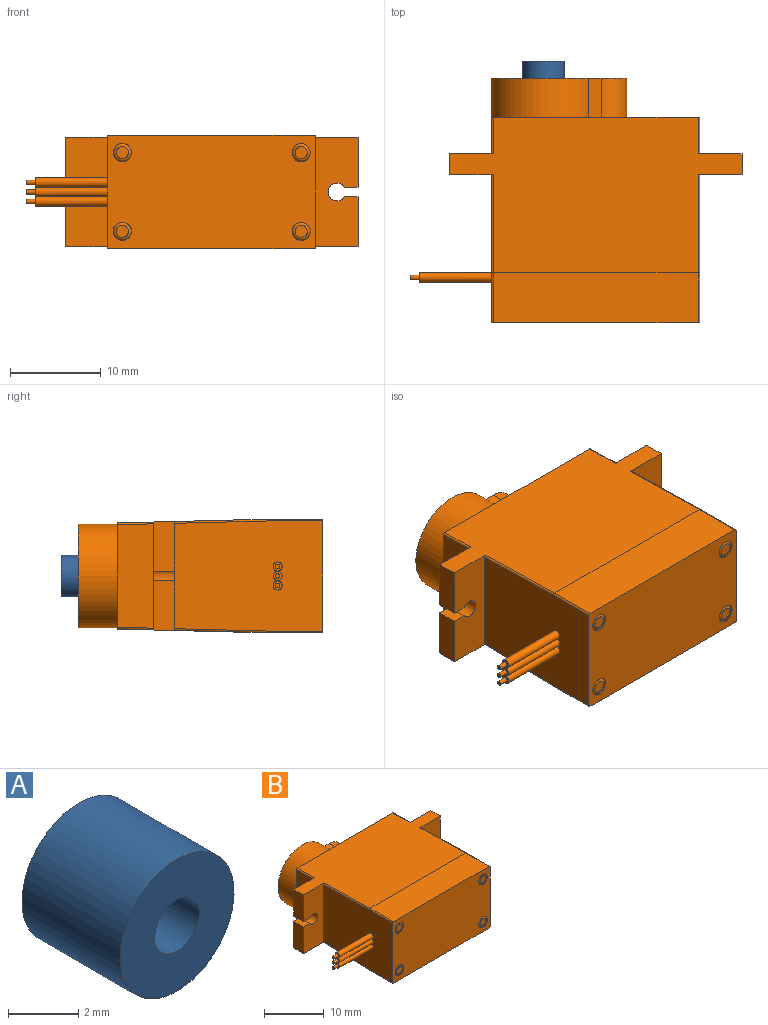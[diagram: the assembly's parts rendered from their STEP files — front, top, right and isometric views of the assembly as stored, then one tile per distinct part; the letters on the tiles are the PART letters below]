
ASSEMBLY  parts=2 mates=1
PART A: 4 faces, bbox 4.6x4x4.6 mm
  f0: cylinder r=2.3mm len=4.6mm, axis (0,1,0), area 57.1mm2, adj f1,f3
  f1: plane 4.6x4.6mm, normal (0,-1,0), area 14.1mm2, adj f0,f2
  f2: cylinder r=0.9mm len=3.95mm, axis (0,1,0), area 22.3mm2, adj f1,f3
  f3: plane 4.6x4.6mm, normal (0,1,0), area 14.1mm2, adj f0,f2
PART B: 75 faces, bbox 36.7x27x12.6 mm
  f0: plane 1x1mm, normal (-1,0,0), area 0.6mm2, adj f50,f55
  f1: plane 1x1mm, normal (-1,0,0), area 0.6mm2, adj f49,f53
  f2: plane 1x1mm, normal (-1,0,0), area 0.6mm2, adj f48,f51
  f3: plane 16.34x12.19mm, normal (-1,0,0), area 193.9mm2, adj f9,f17,f48,f49,f50,f61,f62,f63
  f4: plane 12.04x4.84mm, normal (0,-1,0), area 51.4mm2, adj f5,f13,f14,f24,f25,f29,f30,f31
  f5: plane 5.48x2.32mm, normal (1,0,0), area 12.6mm2, adj f4,f6,f25,f30
  f6: plane 11.93x4.84mm, normal (0,1,0), area 50.8mm2, adj f5,f14,f15,f24,f25,f29,f30,f31
  f7: plane 11.93x4.84mm, normal (0,1,0), area 50.8mm2, adj f8,f11,f12,f24,f25,f26,f27,f28
  f8: plane 5.48x2.32mm, normal (-1,0,0), area 12.6mm2, adj f7,f9,f24,f27
  f9: plane 12.04x4.84mm, normal (0,-1,0), area 51.4mm2, adj f3,f8,f12,f24,f25,f26,f27,f28
  f10: plane 23.03x11.72mm, normal (0,1,0), area 149mm2, adj f11,f15,f19,f20,f21,f22,f24,f25
  f11: plane 11.53x4.06mm, normal (-1,0,0), area 46.4mm2, adj f7,f10,f71,f72
  f12: plane 5.48x2.32mm, normal (-1,0,0), area 12.6mm2, adj f7,f9,f25,f28
  f13: plane 16.34x12.19mm, normal (1,0,0), area 196.2mm2, adj f4,f17,f65,f66,f67,f68
  f14: plane 5.48x2.32mm, normal (1,0,0), area 12.6mm2, adj f4,f6,f24,f31
  f15: plane 11.53x4.06mm, normal (1,0,0), area 46.4mm2, adj f6,f10,f69,f70
  f16: plane 22.63x5.5mm, normal (0,0,1), area 124.5mm2, adj f17,f25,f61,f65
  f17: plane 23.03x12.59mm, normal (0,-1,0), area 277.3mm2, adj f3,f13,f16,f18,f32,f36,f40,f44
  f18: plane 22.63x5.5mm, normal (0,0,-1), area 124.5mm2, adj f17,f24,f63,f67
  f19: cylinder r=5.72mm len=11.45mm, axis (0,-1,0), area 128.4mm2, adj f10,f20,f22,f23
  f20: plane 4.28x1.41mm, normal (0,0,1), area 6mm2, adj f10,f19,f21,f23
  f21: cylinder r=2.85mm len=5.7mm, axis (0,-1,0), area 38.3mm2, adj f10,f20,f22,f23
  f22: plane 4.28x1.41mm, normal (0,0,-1), area 6mm2, adj f10,f19,f21,f23
  f23: plane 14.95x11.45mm, normal (0,1,0), area 103.5mm2, adj f19,f20,f21,f22,f73
  f24: plane 32.31x17.22mm, normal (0,0.03,-1), area 412.3mm2, adj f4,f6,f7,f8,f9,f10,f14,f18
  f25: plane 32.31x17.22mm, normal (0,0.03,1), area 412.3mm2, adj f4,f5,f6,f7,f9,f10,f12,f16
  f26: cylinder r=0.97mm len=2.32mm, axis (0,-1,0), area 11.5mm2, adj f7,f9,f27,f28
  f27: plane 2.32x1.51mm, normal (0,0,1), area 3.5mm2, adj f7,f8,f9,f26
  f28: plane 2.32x1.51mm, normal (0,0,-1), area 3.5mm2, adj f7,f9,f12,f26
  f29: cylinder r=0.97mm len=2.32mm, axis (0,-1,0), area 11.5mm2, adj f4,f6,f30,f31
  f30: plane 2.32x1.51mm, normal (0,0,-1), area 3.5mm2, adj f4,f5,f6,f29
  f31: plane 2.32x1.51mm, normal (0,0,1), area 3.5mm2, adj f4,f6,f14,f29
  f32: cylinder r=1mm len=2mm, axis (0,-1,0), area 6.3mm2, adj f17,f33
  f33: plane 2x2mm, normal (0,-1,0), area 0.2mm2, adj f32,f34
  f34: cylinder r=0.97mm len=1.95mm, axis (0,-1,0), area 4.3mm2, adj f33,f60
  f35: plane 1.35x1.35mm, normal (0,-1,0), area 1.4mm2, adj f60
  f36: cylinder r=1mm len=2mm, axis (0,-1,0), area 6.3mm2, adj f17,f37
  f37: plane 2x2mm, normal (0,-1,0), area 0.2mm2, adj f36,f38
  f38: cylinder r=0.97mm len=1.95mm, axis (0,-1,0), area 4.3mm2, adj f37,f59
  f39: plane 1.35x1.35mm, normal (0,-1,0), area 1.4mm2, adj f59
  f40: cylinder r=1mm len=2mm, axis (0,-1,0), area 6.3mm2, adj f17,f41
  f41: plane 2x2mm, normal (0,-1,0), area 0.2mm2, adj f40,f42
  f42: cylinder r=0.97mm len=1.95mm, axis (0,-1,0), area 4.3mm2, adj f41,f57
  f43: plane 1.35x1.35mm, normal (0,-1,0), area 1.4mm2, adj f57
  f44: cylinder r=1mm len=2mm, axis (0,-1,0), area 6.3mm2, adj f17,f45
  f45: plane 2x2mm, normal (0,-1,0), area 0.2mm2, adj f44,f46
  f46: cylinder r=0.97mm len=1.95mm, axis (0,-1,0), area 4.3mm2, adj f45,f58
  f47: plane 1.35x1.35mm, normal (0,-1,0), area 1.4mm2, adj f58
  f48: cylinder r=0.5mm len=8mm, axis (1,0,0), area 25.1mm2, adj f2,f3
  f49: cylinder r=0.5mm len=8mm, axis (1,0,0), area 25.1mm2, adj f1,f3
  f50: cylinder r=0.5mm len=8mm, axis (1,0,0), area 25.1mm2, adj f0,f3
  f51: cylinder r=0.25mm len=1mm, axis (1,0,0), area 1.6mm2, adj f2,f52
  f52: plane 0.5x0.5mm, normal (-1,0,0), area 0.2mm2, adj f51
  f53: cylinder r=0.25mm len=1mm, axis (1,0,0), area 1.6mm2, adj f1,f54
  f54: plane 0.5x0.5mm, normal (-1,0,0), area 0.2mm2, adj f53
  f55: cylinder r=0.25mm len=1mm, axis (1,0,0), area 1.6mm2, adj f0,f56
  f56: plane 0.5x0.5mm, normal (-1,0,0), area 0.2mm2, adj f55
  f57: torus R=0.68mm, axis (0,1,0), area 2.6mm2, adj f42,f43
  f58: torus R=0.68mm, axis (0,1,0), area 2.6mm2, adj f46,f47
  f59: torus R=0.68mm, axis (0,1,0), area 2.6mm2, adj f38,f39
  f60: torus R=0.68mm, axis (0,1,0), area 2.6mm2, adj f34,f35
  f61: cylinder r=0.2mm len=5.5mm, axis (0,1,0), area 1.7mm2, adj f3,f16,f17,f62
  f62: cylinder r=0.2mm len=10.85mm, axis (0,1,-0.03), area 3.4mm2, adj f3,f9,f25,f61
  f63: cylinder r=0.2mm len=5.5mm, axis (0,-1,0), area 1.7mm2, adj f3,f17,f18,f64
  f64: cylinder r=0.2mm len=10.85mm, axis (0,-1,-0.03), area 3.4mm2, adj f3,f9,f24,f63
  f65: cylinder r=0.2mm len=5.5mm, axis (0,-1,0), area 1.7mm2, adj f13,f16,f17,f66
  f66: cylinder r=0.2mm len=10.85mm, axis (0,-1,0.03), area 3.4mm2, adj f4,f13,f25,f65
  f67: cylinder r=0.2mm len=5.5mm, axis (0,1,0), area 1.7mm2, adj f13,f17,f18,f68
  f68: cylinder r=0.2mm len=10.85mm, axis (0,1,0.03), area 3.4mm2, adj f4,f13,f24,f67
  f69: cylinder r=0.2mm len=4.07mm, axis (0,1,0.03), area 1.3mm2, adj f6,f10,f15,f24
  f70: cylinder r=0.2mm len=4.07mm, axis (0,-1,0.03), area 1.3mm2, adj f6,f10,f15,f25
  f71: cylinder r=0.2mm len=4.07mm, axis (0,-1,-0.03), area 1.3mm2, adj f7,f10,f11,f24
  f72: cylinder r=0.2mm len=4.07mm, axis (0,1,-0.03), area 1.3mm2, adj f7,f10,f11,f25
  f73: cylinder r=2.35mm len=4.7mm, axis (0,1,0), area 30.3mm2, adj f23,f74
  f74: plane 4.7x4.7mm, normal (0,1,0), area 17.3mm2, adj f73
PLACE A t=(1.36,-10.53,-6.38)mm
PLACE B t=(1.36,-9.48,-6.38)mm
MATE planar B.f19 <-> A.f0  axis (0,1,0) through (-0.04,-0.87,-6.38)mm
